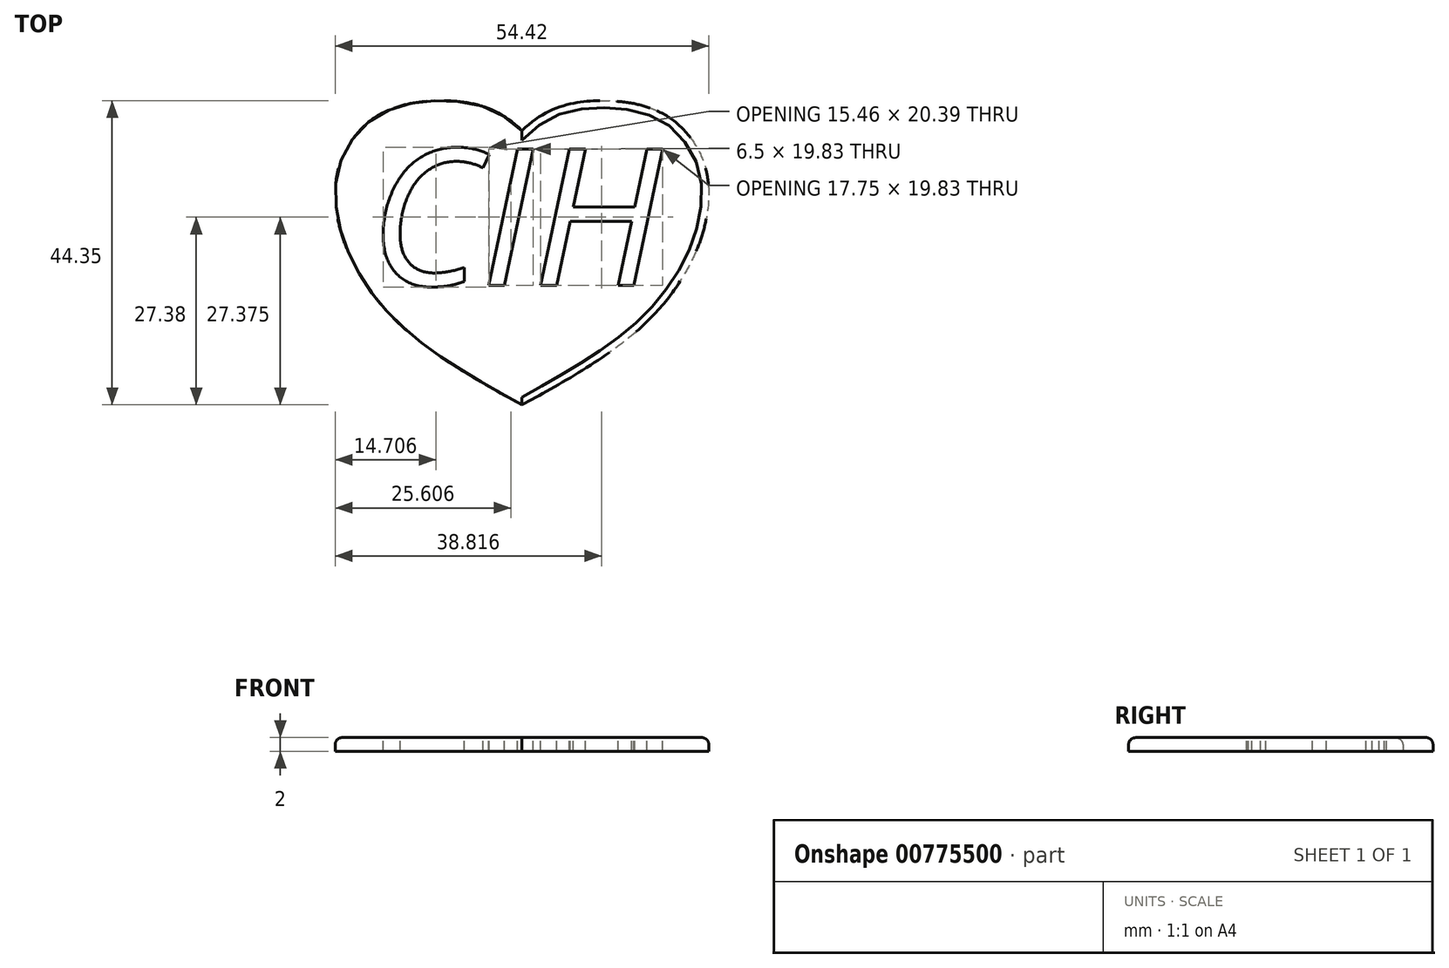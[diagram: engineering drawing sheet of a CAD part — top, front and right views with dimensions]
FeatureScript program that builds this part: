
annotation { "Feature Type Name" : "Feature", "Feature Type Description" : "" }
export const myFeature = defineFeature(function(context is Context, id is Id, definition is map)
    precondition{}
    {
        {
            var Q0;
            Q0=qCreatedBy(makeId("Top.planeOp"),FACE);
            var sketch = newSketch(context, id + "F0", { "sketchPlane" : qUnion([Q0])});
            skFitSpline(sketch, "E0", {"points": [v(0, 40) * mm, v(-12.4, 44.33) * mm, v(-18.67, 43.3) * mm, v(-23.19, 40.5) * mm, v(-26.76, 34.44) * mm, v(-26.76, 26.72) * mm, v(-24.3, 20.2) * mm, v(-19.7, 13.68) * mm, v(-11.24, 6.63) * mm, v(0, 0) * mm], "startDerivative": vector(-89.08, 87.77) * mm, "endDerivative": vector(67.58, -36.73) * mm});
            skLineSegment(sketch, "E1", {"start": v(0, 40) * mm, "end": v(0, 0) * mm});
            skSolve(sketch);
        }
        {
            var Q0;
            Q0=makeQuery(id+"F0.imprint","IMPRINT",FACE,{"disambiguationData":[TD([[makeQuery(id+"F0.imprint","IMPRINT",EDGE,{"derivedFrom":sQuery(id+"F0.wireOp",EDGE,"E0")}),1.0]])]});
            extrude(context, id + "F1", {"entities" : qUnion([Q0]), "depth" : 2 * mm, "offsetDistance" : 25 * mm});
        }
        {
            var Q0;
            Q0=makeQuery(id+"F1.opExtrude","SWEPT_BODY",BODY,{"disambiguationData":[OSD([sQuery(id+"F0.wireOp",EDGE,"E0"),sQuery(id+"F0.wireOp",EDGE,"E1")])]});
            var Q1;
            Q1=makeQuery(id+"F1.opExtrude","SWEPT_FACE",FACE,{"disambiguationData":[OSD([sQuery(id+"F0.wireOp",EDGE,"E1")])]});
            mirror(context, id + "F2", {"operationType" : NewBodyOperationType.ADD, "entities" : qUnion([Q0]), "mirrorPlane" : qUnion([Q1])});
        }
        {
            var Q0;
            {var subQ0=makeQuery(id+"F1.opExtrude","CAP_FACE",FACE,{"disambiguationData":[OSD([sQuery(id+"F0.wireOp",EDGE,"E0"),sQuery(id+"F0.wireOp",EDGE,"E1")])],"isStart":false});Q0=makeQuery(id+"F2.boolean.opBoolean","MERGE",FACE,{"derivedFrom":[subQ0,makeQuery(id+"F2.opPattern","COPY",FACE,{"derivedFrom":subQ0,"instanceName":"1"})]});}
            var sketch = newSketch(context, id + "F3", { "sketchPlane" : qUnion([Q0])});
            skText(sketch, "E2", { "text": "CIH", "fontName": "OpenSans-Italic.ttf"});
            const initialGuessF3  = {"E2": [-0.02227, 0.01746, 1, 0, 0.02]};
            skSetInitialGuess(sketch, initialGuessF3);
            skSolve(sketch);
        }
        {
            var Q0;
            Q0 = qSketchRegion(id + "F3", true);
            extrude(context, id + "F4", {"entities" : qUnion([Q0]), "operationType" : NewBodyOperationType.REMOVE, "oppositeDirection" : true, "depth" : 30 * mm, "offsetDistance" : 25 * mm});
        }
        {
            var Q0;
            Q0=makeQuery(id+"F2.opPattern","COPY",EDGE,{"derivedFrom":makeQuery(id+"F1.opExtrude","CAP_EDGE",EDGE,{"disambiguationData":[OSD([sQuery(id+"F0.wireOp",EDGE,"E0")])],"isStart":false}),"instanceName":"1"});
            var Q1;
            Q1=makeQuery(id+"F4.boolean.opBoolean","COPY",EDGE,{"derivedFrom":makeQuery(id+"F4.opExtrude","CAP_EDGE",EDGE,{"disambiguationData":[OSD([sQuery(id+"F3.wireOp",EDGE,"E2.sketch_text.stroke-37")])],"isStart":true})});
            var Q2;
            Q2=makeQuery(id+"F4.boolean.opBoolean","COPY",EDGE,{"derivedFrom":makeQuery(id+"F4.opExtrude","CAP_EDGE",EDGE,{"disambiguationData":[OSD([sQuery(id+"F3.wireOp",EDGE,"E2.sketch_text.stroke-3")])],"isStart":true})});
            var Q3;
            Q3=makeQuery(id+"F4.boolean.opBoolean","COPY",EDGE,{"derivedFrom":makeQuery(id+"F4.opExtrude","CAP_EDGE",EDGE,{"disambiguationData":[OSD([sQuery(id+"F3.wireOp",EDGE,"E2.sketch_text.stroke-54")])],"isStart":true})});
            var Q4;
            Q4=makeQuery(id+"F1.opExtrude","CAP_EDGE",EDGE,{"disambiguationData":[OSD([sQuery(id+"F0.wireOp",EDGE,"E0")])],"isStart":false});
            var Q5;
            Q5=makeQuery(id+"F4.boolean.opBoolean","COPY",EDGE,{"derivedFrom":makeQuery(id+"F4.opExtrude","CAP_EDGE",EDGE,{"disambiguationData":[OSD([sQuery(id+"F3.wireOp",EDGE,"E2.sketch_text.stroke-12")])],"isStart":true})});
            var Q6;
            Q6=makeQuery(id+"F4.boolean.opBoolean","COPY",EDGE,{"derivedFrom":makeQuery(id+"F4.opExtrude","CAP_EDGE",EDGE,{"disambiguationData":[OSD([sQuery(id+"F3.wireOp",EDGE,"E2.sketch_text.stroke-8")])],"isStart":true})});
            var Q7;
            Q7=makeQuery(id+"F4.boolean.opBoolean","COPY",EDGE,{"derivedFrom":makeQuery(id+"F4.opExtrude","CAP_EDGE",EDGE,{"disambiguationData":[OSD([sQuery(id+"F3.wireOp",EDGE,"E2.sketch_text.stroke-26")])],"isStart":true})});
            var Q8;
            Q8=makeQuery(id+"F4.boolean.opBoolean","COPY",EDGE,{"derivedFrom":makeQuery(id+"F4.opExtrude","CAP_EDGE",EDGE,{"disambiguationData":[OSD([sQuery(id+"F3.wireOp",EDGE,"E2.sketch_text.stroke-60")])],"isStart":true})});
            var Q9;
            Q9=makeQuery(id+"F4.boolean.opBoolean","COPY",EDGE,{"derivedFrom":makeQuery(id+"F4.opExtrude","CAP_EDGE",EDGE,{"disambiguationData":[OSD([sQuery(id+"F3.wireOp",EDGE,"E2.sketch_text.stroke-32")])],"isStart":true})});
            var Q10;
            Q10=makeQuery(id+"F4.boolean.opBoolean","COPY",EDGE,{"derivedFrom":makeQuery(id+"F4.opExtrude","CAP_EDGE",EDGE,{"disambiguationData":[OSD([sQuery(id+"F3.wireOp",EDGE,"E2.sketch_text.stroke-51")])],"isStart":true})});
            var Q11;
            Q11=makeQuery(id+"F4.boolean.opBoolean","COPY",EDGE,{"derivedFrom":makeQuery(id+"F4.opExtrude","CAP_EDGE",EDGE,{"disambiguationData":[OSD([sQuery(id+"F3.wireOp",EDGE,"E2.sketch_text.stroke-20")])],"isStart":true})});
            var Q12;
            Q12=makeQuery(id+"F4.boolean.opBoolean","COPY",EDGE,{"derivedFrom":makeQuery(id+"F4.opExtrude","CAP_EDGE",EDGE,{"disambiguationData":[OSD([sQuery(id+"F3.wireOp",EDGE,"E2.sketch_text.stroke-25")])],"isStart":true})});
            var Q13;
            Q13=makeQuery(id+"F4.boolean.opBoolean","COPY",EDGE,{"derivedFrom":makeQuery(id+"F4.opExtrude","CAP_EDGE",EDGE,{"disambiguationData":[OSD([sQuery(id+"F3.wireOp",EDGE,"E2.sketch_text.stroke-46")])],"isStart":true})});
            var Q14;
            Q14=makeQuery(id+"F4.boolean.opBoolean","COPY",EDGE,{"derivedFrom":makeQuery(id+"F4.opExtrude","CAP_EDGE",EDGE,{"disambiguationData":[OSD([sQuery(id+"F3.wireOp",EDGE,"E2.sketch_text.stroke-62")])],"isStart":true})});
            var Q15;
            Q15=makeQuery(id+"F4.boolean.opBoolean","COPY",EDGE,{"derivedFrom":makeQuery(id+"F4.opExtrude","CAP_EDGE",EDGE,{"disambiguationData":[OSD([sQuery(id+"F3.wireOp",EDGE,"E2.sketch_text.stroke-0")])],"isStart":true})});
            var Q16;
            Q16=makeQuery(id+"F4.boolean.opBoolean","COPY",EDGE,{"derivedFrom":makeQuery(id+"F4.opExtrude","CAP_EDGE",EDGE,{"disambiguationData":[OSD([sQuery(id+"F3.wireOp",EDGE,"E2.sketch_text.stroke-52")])],"isStart":true})});
            var Q17;
            Q17=makeQuery(id+"F4.boolean.opBoolean","COPY",EDGE,{"derivedFrom":makeQuery(id+"F4.opExtrude","CAP_EDGE",EDGE,{"disambiguationData":[OSD([sQuery(id+"F3.wireOp",EDGE,"E2.sketch_text.stroke-28")])],"isStart":true})});
            var Q18;
            Q18=makeQuery(id+"F4.boolean.opBoolean","COPY",EDGE,{"derivedFrom":makeQuery(id+"F4.opExtrude","CAP_EDGE",EDGE,{"disambiguationData":[OSD([sQuery(id+"F3.wireOp",EDGE,"E2.sketch_text.stroke-2")])],"isStart":true})});
            var Q19;
            Q19=makeQuery(id+"F4.boolean.opBoolean","COPY",EDGE,{"derivedFrom":makeQuery(id+"F4.opExtrude","CAP_EDGE",EDGE,{"disambiguationData":[OSD([sQuery(id+"F3.wireOp",EDGE,"E2.sketch_text.stroke-15")])],"isStart":true})});
            var Q20;
            Q20=makeQuery(id+"F4.boolean.opBoolean","COPY",EDGE,{"derivedFrom":makeQuery(id+"F4.opExtrude","CAP_EDGE",EDGE,{"disambiguationData":[OSD([sQuery(id+"F3.wireOp",EDGE,"E2.sketch_text.stroke-43")])],"isStart":true})});
            var Q21;
            Q21=makeQuery(id+"F4.boolean.opBoolean","COPY",EDGE,{"derivedFrom":makeQuery(id+"F4.opExtrude","CAP_EDGE",EDGE,{"disambiguationData":[OSD([sQuery(id+"F3.wireOp",EDGE,"E2.sketch_text.stroke-55")])],"isStart":true})});
            var Q22;
            Q22=makeQuery(id+"F4.boolean.opBoolean","COPY",EDGE,{"derivedFrom":makeQuery(id+"F4.opExtrude","CAP_EDGE",EDGE,{"disambiguationData":[OSD([sQuery(id+"F3.wireOp",EDGE,"E2.sketch_text.stroke-59")])],"isStart":true})});
            var Q23;
            Q23=makeQuery(id+"F4.boolean.opBoolean","COPY",EDGE,{"derivedFrom":makeQuery(id+"F4.opExtrude","CAP_EDGE",EDGE,{"disambiguationData":[OSD([sQuery(id+"F3.wireOp",EDGE,"E2.sketch_text.stroke-47")])],"isStart":true})});
            var Q24;
            Q24=makeQuery(id+"F4.boolean.opBoolean","COPY",EDGE,{"derivedFrom":makeQuery(id+"F4.opExtrude","CAP_EDGE",EDGE,{"disambiguationData":[OSD([sQuery(id+"F3.wireOp",EDGE,"E2.sketch_text.stroke-5")])],"isStart":true})});
            var Q25;
            Q25=makeQuery(id+"F4.boolean.opBoolean","COPY",EDGE,{"derivedFrom":makeQuery(id+"F4.opExtrude","CAP_EDGE",EDGE,{"disambiguationData":[OSD([sQuery(id+"F3.wireOp",EDGE,"E2.sketch_text.stroke-45")])],"isStart":true})});
            var Q26;
            Q26=makeQuery(id+"F4.boolean.opBoolean","COPY",EDGE,{"derivedFrom":makeQuery(id+"F4.opExtrude","CAP_EDGE",EDGE,{"disambiguationData":[OSD([sQuery(id+"F3.wireOp",EDGE,"E2.sketch_text.stroke-44")])],"isStart":true})});
            var Q27;
            Q27=makeQuery(id+"F4.boolean.opBoolean","COPY",EDGE,{"derivedFrom":makeQuery(id+"F4.opExtrude","CAP_EDGE",EDGE,{"disambiguationData":[OSD([sQuery(id+"F3.wireOp",EDGE,"E2.sketch_text.stroke-4")])],"isStart":true})});
            var Q28;
            Q28=makeQuery(id+"F4.boolean.opBoolean","COPY",EDGE,{"derivedFrom":makeQuery(id+"F4.opExtrude","CAP_EDGE",EDGE,{"disambiguationData":[OSD([sQuery(id+"F3.wireOp",EDGE,"E2.sketch_text.stroke-42")])],"isStart":true})});
            var Q29;
            Q29=makeQuery(id+"F4.boolean.opBoolean","COPY",EDGE,{"derivedFrom":makeQuery(id+"F4.opExtrude","CAP_EDGE",EDGE,{"disambiguationData":[OSD([sQuery(id+"F3.wireOp",EDGE,"E2.sketch_text.stroke-57")])],"isStart":true})});
            var Q30;
            Q30=makeQuery(id+"F4.boolean.opBoolean","COPY",EDGE,{"derivedFrom":makeQuery(id+"F4.opExtrude","CAP_EDGE",EDGE,{"disambiguationData":[OSD([sQuery(id+"F3.wireOp",EDGE,"E2.sketch_text.stroke-22")])],"isStart":true})});
            var Q31;
            Q31=makeQuery(id+"F4.boolean.opBoolean","COPY",EDGE,{"derivedFrom":makeQuery(id+"F4.opExtrude","CAP_EDGE",EDGE,{"disambiguationData":[OSD([sQuery(id+"F3.wireOp",EDGE,"E2.sketch_text.stroke-18")])],"isStart":true})});
            var Q32;
            Q32=makeQuery(id+"F4.boolean.opBoolean","COPY",EDGE,{"derivedFrom":makeQuery(id+"F4.opExtrude","CAP_EDGE",EDGE,{"disambiguationData":[OSD([sQuery(id+"F3.wireOp",EDGE,"E2.sketch_text.stroke-1")])],"isStart":true})});
            var Q33;
            Q33=makeQuery(id+"F4.boolean.opBoolean","COPY",EDGE,{"derivedFrom":makeQuery(id+"F4.opExtrude","CAP_EDGE",EDGE,{"disambiguationData":[OSD([sQuery(id+"F3.wireOp",EDGE,"E2.sketch_text.stroke-7")])],"isStart":true})});
            var Q34;
            Q34=makeQuery(id+"F4.boolean.opBoolean","COPY",EDGE,{"derivedFrom":makeQuery(id+"F4.opExtrude","CAP_EDGE",EDGE,{"disambiguationData":[OSD([sQuery(id+"F3.wireOp",EDGE,"E2.sketch_text.stroke-9")])],"isStart":true})});
            var Q35;
            Q35=makeQuery(id+"F4.boolean.opBoolean","COPY",EDGE,{"derivedFrom":makeQuery(id+"F4.opExtrude","CAP_EDGE",EDGE,{"disambiguationData":[OSD([sQuery(id+"F3.wireOp",EDGE,"E2.sketch_text.stroke-11")])],"isStart":true})});
            var Q36;
            Q36=makeQuery(id+"F4.boolean.opBoolean","COPY",EDGE,{"derivedFrom":makeQuery(id+"F4.opExtrude","CAP_EDGE",EDGE,{"disambiguationData":[OSD([sQuery(id+"F3.wireOp",EDGE,"E2.sketch_text.stroke-6")])],"isStart":true})});
            var Q37;
            Q37=makeQuery(id+"F4.boolean.opBoolean","COPY",EDGE,{"derivedFrom":makeQuery(id+"F4.opExtrude","CAP_EDGE",EDGE,{"disambiguationData":[OSD([sQuery(id+"F3.wireOp",EDGE,"E2.sketch_text.stroke-53")])],"isStart":true})});
            var Q38;
            Q38=makeQuery(id+"F4.boolean.opBoolean","COPY",EDGE,{"derivedFrom":makeQuery(id+"F4.opExtrude","CAP_EDGE",EDGE,{"disambiguationData":[OSD([sQuery(id+"F3.wireOp",EDGE,"E2.sketch_text.stroke-38")])],"isStart":true})});
            var Q39;
            Q39=makeQuery(id+"F4.boolean.opBoolean","COPY",EDGE,{"derivedFrom":makeQuery(id+"F4.opExtrude","CAP_EDGE",EDGE,{"disambiguationData":[OSD([sQuery(id+"F3.wireOp",EDGE,"E2.sketch_text.stroke-24")])],"isStart":true})});
            var Q40;
            Q40=makeQuery(id+"F4.boolean.opBoolean","COPY",EDGE,{"derivedFrom":makeQuery(id+"F4.opExtrude","CAP_EDGE",EDGE,{"disambiguationData":[OSD([sQuery(id+"F3.wireOp",EDGE,"E2.sketch_text.stroke-58")])],"isStart":true})});
            var Q41;
            Q41=makeQuery(id+"F4.boolean.opBoolean","COPY",EDGE,{"derivedFrom":makeQuery(id+"F4.opExtrude","CAP_EDGE",EDGE,{"disambiguationData":[OSD([sQuery(id+"F3.wireOp",EDGE,"E2.sketch_text.stroke-61")])],"isStart":true})});
            var Q42;
            Q42=makeQuery(id+"F4.boolean.opBoolean","COPY",EDGE,{"derivedFrom":makeQuery(id+"F4.opExtrude","CAP_EDGE",EDGE,{"disambiguationData":[OSD([sQuery(id+"F3.wireOp",EDGE,"E2.sketch_text.stroke-41")])],"isStart":true})});
            var Q43;
            Q43=makeQuery(id+"F4.boolean.opBoolean","COPY",EDGE,{"derivedFrom":makeQuery(id+"F4.opExtrude","CAP_EDGE",EDGE,{"disambiguationData":[OSD([sQuery(id+"F3.wireOp",EDGE,"E2.sketch_text.stroke-14")])],"isStart":true})});
            var Q44;
            Q44=makeQuery(id+"F4.boolean.opBoolean","COPY",EDGE,{"derivedFrom":makeQuery(id+"F4.opExtrude","CAP_EDGE",EDGE,{"disambiguationData":[OSD([sQuery(id+"F3.wireOp",EDGE,"E2.sketch_text.stroke-36")])],"isStart":true})});
            var Q45;
            Q45=makeQuery(id+"F4.boolean.opBoolean","COPY",EDGE,{"derivedFrom":makeQuery(id+"F4.opExtrude","CAP_EDGE",EDGE,{"disambiguationData":[OSD([sQuery(id+"F3.wireOp",EDGE,"E2.sketch_text.stroke-50")])],"isStart":true})});
            var Q46;
            Q46=makeQuery(id+"F4.boolean.opBoolean","COPY",EDGE,{"derivedFrom":makeQuery(id+"F4.opExtrude","CAP_EDGE",EDGE,{"disambiguationData":[OSD([sQuery(id+"F3.wireOp",EDGE,"E2.sketch_text.stroke-27")])],"isStart":true})});
            var Q47;
            Q47=makeQuery(id+"F4.boolean.opBoolean","COPY",EDGE,{"derivedFrom":makeQuery(id+"F4.opExtrude","CAP_EDGE",EDGE,{"disambiguationData":[OSD([sQuery(id+"F3.wireOp",EDGE,"E2.sketch_text.stroke-48")])],"isStart":true})});
            var Q48;
            Q48=makeQuery(id+"F4.boolean.opBoolean","COPY",EDGE,{"derivedFrom":makeQuery(id+"F4.opExtrude","CAP_EDGE",EDGE,{"disambiguationData":[OSD([sQuery(id+"F3.wireOp",EDGE,"E2.sketch_text.stroke-13")])],"isStart":true})});
            var Q49;
            Q49=makeQuery(id+"F4.boolean.opBoolean","COPY",EDGE,{"derivedFrom":makeQuery(id+"F4.opExtrude","CAP_EDGE",EDGE,{"disambiguationData":[OSD([sQuery(id+"F3.wireOp",EDGE,"E2.sketch_text.stroke-56")])],"isStart":true})});
            var Q50;
            Q50=makeQuery(id+"F4.boolean.opBoolean","COPY",EDGE,{"derivedFrom":makeQuery(id+"F4.opExtrude","CAP_EDGE",EDGE,{"disambiguationData":[OSD([sQuery(id+"F3.wireOp",EDGE,"E2.sketch_text.stroke-35")])],"isStart":true})});
            var Q51;
            Q51=makeQuery(id+"F4.boolean.opBoolean","COPY",EDGE,{"derivedFrom":makeQuery(id+"F4.opExtrude","CAP_EDGE",EDGE,{"disambiguationData":[OSD([sQuery(id+"F3.wireOp",EDGE,"E2.sketch_text.stroke-29")])],"isStart":true})});
            var Q52;
            Q52=makeQuery(id+"F4.boolean.opBoolean","COPY",EDGE,{"derivedFrom":makeQuery(id+"F4.opExtrude","CAP_EDGE",EDGE,{"disambiguationData":[OSD([sQuery(id+"F3.wireOp",EDGE,"E2.sketch_text.stroke-21")])],"isStart":true})});
            var Q53;
            Q53=makeQuery(id+"F4.boolean.opBoolean","COPY",EDGE,{"derivedFrom":makeQuery(id+"F4.opExtrude","CAP_EDGE",EDGE,{"disambiguationData":[OSD([sQuery(id+"F3.wireOp",EDGE,"E2.sketch_text.stroke-49")])],"isStart":true})});
            var Q54;
            Q54=makeQuery(id+"F4.boolean.opBoolean","COPY",EDGE,{"derivedFrom":makeQuery(id+"F4.opExtrude","CAP_EDGE",EDGE,{"disambiguationData":[OSD([sQuery(id+"F3.wireOp",EDGE,"E2.sketch_text.stroke-30")])],"isStart":true})});
            var Q55;
            Q55=makeQuery(id+"F4.boolean.opBoolean","COPY",EDGE,{"derivedFrom":makeQuery(id+"F4.opExtrude","CAP_EDGE",EDGE,{"disambiguationData":[OSD([sQuery(id+"F3.wireOp",EDGE,"E2.sketch_text.stroke-34")])],"isStart":true})});
            var Q56;
            Q56=makeQuery(id+"F4.boolean.opBoolean","COPY",EDGE,{"derivedFrom":makeQuery(id+"F4.opExtrude","CAP_EDGE",EDGE,{"disambiguationData":[OSD([sQuery(id+"F3.wireOp",EDGE,"E2.sketch_text.stroke-31")])],"isStart":true})});
            var Q57;
            Q57=makeQuery(id+"F4.boolean.opBoolean","COPY",EDGE,{"derivedFrom":makeQuery(id+"F4.opExtrude","CAP_EDGE",EDGE,{"disambiguationData":[OSD([sQuery(id+"F3.wireOp",EDGE,"E2.sketch_text.stroke-10")])],"isStart":true})});
            var Q58;
            Q58=makeQuery(id+"F4.boolean.opBoolean","COPY",EDGE,{"derivedFrom":makeQuery(id+"F4.opExtrude","CAP_EDGE",EDGE,{"disambiguationData":[OSD([sQuery(id+"F3.wireOp",EDGE,"E2.sketch_text.stroke-16")])],"isStart":true})});
            var Q59;
            Q59=makeQuery(id+"F4.boolean.opBoolean","COPY",EDGE,{"derivedFrom":makeQuery(id+"F4.opExtrude","CAP_EDGE",EDGE,{"disambiguationData":[OSD([sQuery(id+"F3.wireOp",EDGE,"E2.sketch_text.stroke-19")])],"isStart":true})});
            var Q60;
            Q60=makeQuery(id+"F4.boolean.opBoolean","COPY",EDGE,{"derivedFrom":makeQuery(id+"F4.opExtrude","CAP_EDGE",EDGE,{"disambiguationData":[OSD([sQuery(id+"F3.wireOp",EDGE,"E2.sketch_text.stroke-17")])],"isStart":true})});
            var Q61;
            Q61=makeQuery(id+"F4.boolean.opBoolean","COPY",EDGE,{"derivedFrom":makeQuery(id+"F4.opExtrude","CAP_EDGE",EDGE,{"disambiguationData":[OSD([sQuery(id+"F3.wireOp",EDGE,"E2.sketch_text.stroke-33")])],"isStart":true})});
            var Q62;
            Q62=makeQuery(id+"F4.boolean.opBoolean","COPY",EDGE,{"derivedFrom":makeQuery(id+"F4.opExtrude","CAP_EDGE",EDGE,{"disambiguationData":[OSD([sQuery(id+"F3.wireOp",EDGE,"E2.sketch_text.stroke-39")])],"isStart":true})});
            var Q63;
            Q63=makeQuery(id+"F4.boolean.opBoolean","COPY",EDGE,{"derivedFrom":makeQuery(id+"F4.opExtrude","CAP_EDGE",EDGE,{"disambiguationData":[OSD([sQuery(id+"F3.wireOp",EDGE,"E2.sketch_text.stroke-23")])],"isStart":true})});
            var Q64;
            Q64=makeQuery(id+"F4.boolean.opBoolean","COPY",EDGE,{"derivedFrom":makeQuery(id+"F4.opExtrude","CAP_EDGE",EDGE,{"disambiguationData":[OSD([sQuery(id+"F3.wireOp",EDGE,"E2.sketch_text.stroke-40")])],"isStart":true})});
            fillet(context, id + "F5", {"entities" : qUnion([Q0, Q1, Q2, Q3, Q4, Q5, Q6, Q7, Q8, Q9, Q10, Q11, Q12, Q13, Q14, Q15, Q16, Q17, Q18, Q19, Q20, Q21, Q22, Q23, Q24, Q25, Q26, Q27, Q28, Q29, Q30, Q31, Q32, Q33, Q34, Q35, Q36, Q37, Q38, Q39, Q40, Q41, Q42, Q43, Q44, Q45, Q46, Q47, Q48, Q49, Q50, Q51, Q52, Q53, Q54, Q55, Q56, Q57, Q58, Q59, Q60, Q61, Q62, Q63, Q64]), "radius" : 1 * mm, "tangentPropagation" : true, "allowEdgeOverflow" : false});
        }
    });
